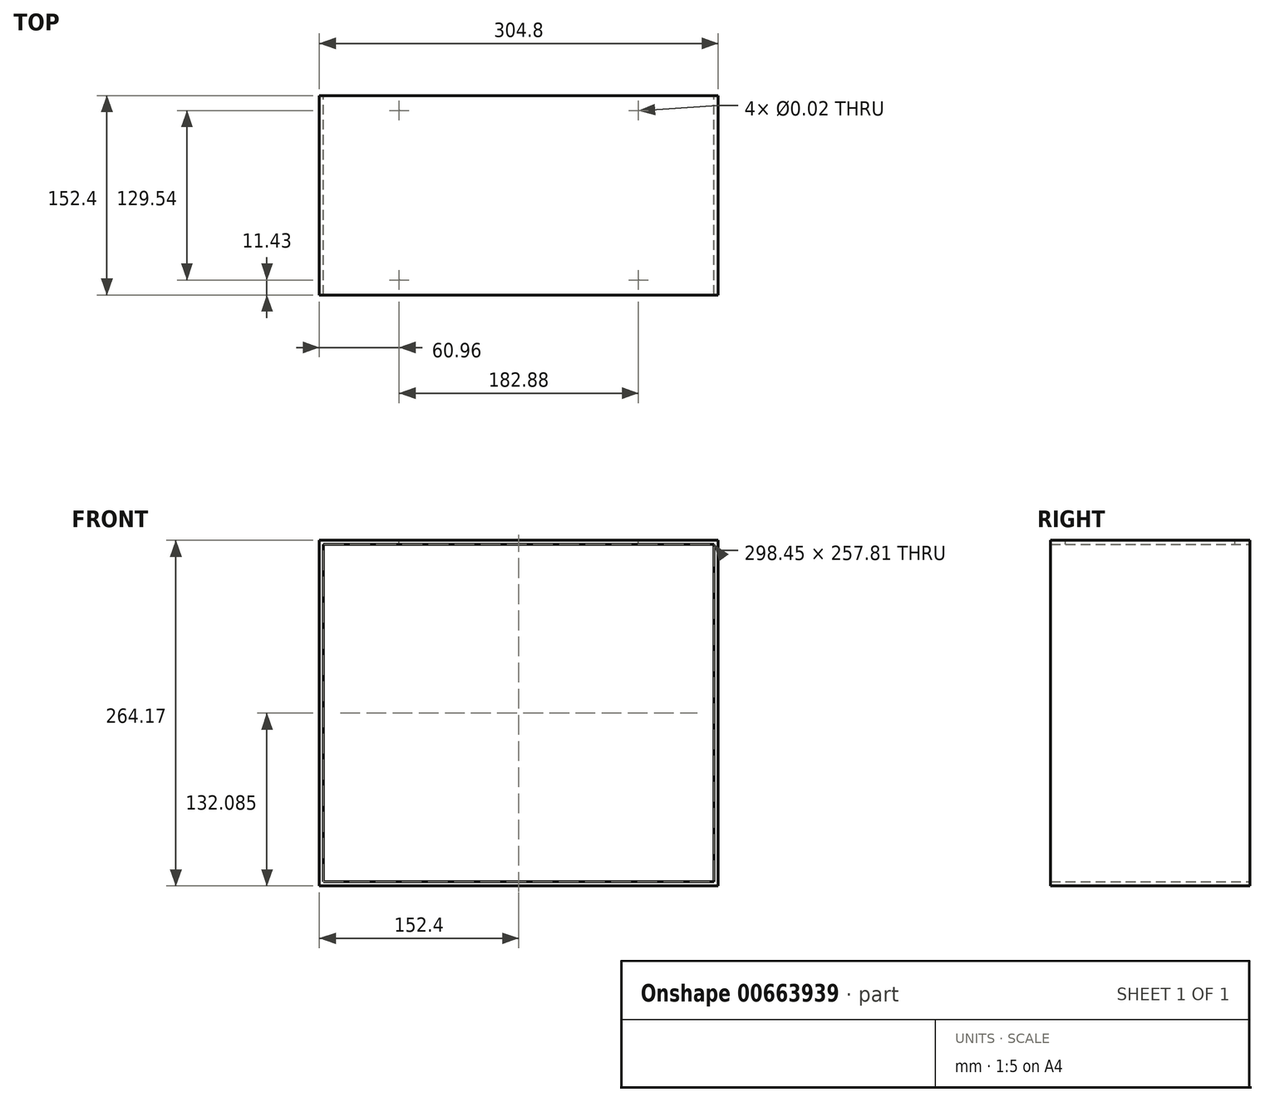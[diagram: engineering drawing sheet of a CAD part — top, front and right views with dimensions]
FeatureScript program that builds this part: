
annotation { "Feature Type Name" : "Feature", "Feature Type Description" : "" }
export const myFeature = defineFeature(function(context is Context, id is Id, definition is map)
    precondition{}
    {
        {
            var Q0;
            Q0=qCreatedBy(makeId("Top.planeOp"),FACE);
            var sketch = newSketch(context, id + "F0", { "sketchPlane" : qUnion([Q0])});
            skLineSegment(sketch, "E0.bottom", {"start": v(-152.4, 76.2) * mm, "end": v(152.4, 76.2) * mm});
            skLineSegment(sketch, "E0.top", {"start": v(-152.4, -76.2) * mm, "end": v(152.4, -76.2) * mm});
            skLineSegment(sketch, "E0.left", {"start": v(-152.4, 76.2) * mm, "end": v(-152.4, -76.2) * mm});
            skLineSegment(sketch, "E0.right", {"start": v(152.4, 76.2) * mm, "end": v(152.4, -76.2) * mm});
            skSolve(sketch);
        }
        {
            var Q0;
            Q0 = qSketchRegion(id + "F0", true);
            extrude(context, id + "F1", {"entities" : qUnion([Q0]), "depth" : 3.17 * mm, "offsetDistance" : 25.4 * mm});
        }
        {
            var Q0;
            Q0=makeQuery(id+"F1.opExtrude","CAP_FACE",FACE,{"disambiguationData":[OSD([sQuery(id+"F0.wireOp",EDGE,"E0.bottom"),sQuery(id+"F0.wireOp",EDGE,"E0.top"),sQuery(id+"F0.wireOp",EDGE,"E0.left"),sQuery(id+"F0.wireOp",EDGE,"E0.right")])],"isStart":false});
            var sketch = newSketch(context, id + "F2", { "sketchPlane" : qUnion([Q0])});
            skLineSegment(sketch, "E1.bottom", {"start": v(-107.95, 82.55) * mm, "end": v(107.95, 82.55) * mm});
            skLineSegment(sketch, "E1.top", {"start": v(-107.95, -82.55) * mm, "end": v(107.95, -82.55) * mm});
            skLineSegment(sketch, "E1.left", {"start": v(-107.95, 82.55) * mm, "end": v(-107.95, -82.55) * mm});
            skLineSegment(sketch, "E1.right", {"start": v(107.95, 82.55) * mm, "end": v(107.95, -82.55) * mm});
            skSolve(sketch);
        }
        {
            var Q0;
            {var subQ0=sQuery(id+"F2.wireOp",EDGE,"E1.left");var subQ1=makeQuery(id+"F1.opExtrude","CAP_EDGE",EDGE,{"disambiguationData":[OSD([sQuery(id+"F0.wireOp",EDGE,"E0.bottom")])],"isStart":false});var subQ2=makeQuery(id+"F2.imprint","INTERSECT",VERTEX,{"derivedFrom":[subQ1,subQ0]});Q0=makeQuery(id+"F2.imprint","IMPRINT",FACE,{"disambiguationData":[TD([[makeQuery(id+"F2.imprint","IMPRINT",EDGE,{"disambiguationData":[TD([[subQ2,-1.0]])],"derivedFrom":subQ0}),1.0]])]});}
            var sketch = newSketch(context, id + "F3", { "sketchPlane" : qUnion([Q0])});
            skPoint(sketch, "E2", {"position": v(-91.44, 64.77) * mm});
            skPoint(sketch, "E3", {"position": v(-91.44, -64.77) * mm});
            skPoint(sketch, "E4.MirrorP", {"position": v(91.44, -64.77) * mm});
            skPoint(sketch, "E5.MirrorP", {"position": v(91.44, 64.77) * mm});
            skSolve(sketch);
        }
        {
            var Q0;
            Q0=sQuery(id+"F3.wireOp",VERTEX,"E2");
            var Q1;
            Q1=sQuery(id+"F3.wireOp",VERTEX,"E3");
            var Q2;
            Q2=sQuery(id+"F3.wireOp",VERTEX,"E4.MirrorP");
            var Q3;
            Q3=sQuery(id+"F3.wireOp",VERTEX,"E5.MirrorP");
            var Q4;
            Q4=makeQuery(id+"F1.opExtrude","SWEPT_BODY",BODY,{"disambiguationData":[OSD([sQuery(id+"F0.wireOp",EDGE,"E0.bottom"),sQuery(id+"F0.wireOp",EDGE,"E0.top"),sQuery(id+"F0.wireOp",EDGE,"E0.left"),sQuery(id+"F0.wireOp",EDGE,"E0.right")])]});
            hole(context, id + "F4", {"style" : HoleStyle.SIMPLE, "endStyle" : HoleEndStyle.THROUGH, "standardTappedOrClearance" : lookupTablePath({ "standard" : "ANSI", "size" : "1/2 (0.5)", "type" : "Drilled" }), "standardBlindInLast" : lookupTablePath({ "standard" : "ANSI", "size" : "1/2", "type" : "Drilled" }), "holeDiameter" : 1 / 50.8 * mm, "majorDiameter" : 6.35 * mm, "isTappedThrough" : true, "tappedDepth" : 12.7 * mm, "tapClearance" : 3, "locations" : qUnion([Q0, Q1, Q2, Q3]), "scope" : qUnion([Q4])});
        }
        {
            var Q0;
            Q0=makeQuery(id+"F1.opExtrude","CAP_FACE",FACE,{"disambiguationData":[OSD([sQuery(id+"F0.wireOp",EDGE,"E0.bottom"),sQuery(id+"F0.wireOp",EDGE,"E0.top"),sQuery(id+"F0.wireOp",EDGE,"E0.left"),sQuery(id+"F0.wireOp",EDGE,"E0.right")])],"isStart":true});
            var sketch = newSketch(context, id + "F5", { "sketchPlane" : qUnion([Q0])});
            skLineSegment(sketch, "E6.bottom", {"start": v(-152.4, 76.2) * mm, "end": v(-149.22, 76.2) * mm});
            skLineSegment(sketch, "E6.top", {"start": v(-152.4, -76.2) * mm, "end": v(-149.22, -76.2) * mm});
            skLineSegment(sketch, "E6.left", {"start": v(-152.4, 76.2) * mm, "end": v(-152.4, -76.2) * mm});
            skLineSegment(sketch, "E6.right", {"start": v(-149.22, 76.2) * mm, "end": v(-149.22, -76.2) * mm});
            skLineSegment(sketch, "E7.MirrorCS", {"start": v(152.4, 76.2) * mm, "end": v(149.22, 76.2) * mm});
            skLineSegment(sketch, "E8.MirrorCS", {"start": v(152.4, -76.2) * mm, "end": v(149.22, -76.2) * mm});
            skLineSegment(sketch, "E9.MirrorCS", {"start": v(152.4, 76.2) * mm, "end": v(152.4, -76.2) * mm});
            skLineSegment(sketch, "E10.MirrorCS", {"start": v(149.22, 76.2) * mm, "end": v(149.22, -76.2) * mm});
            skSolve(sketch);
        }
        {
            var Q0;
            Q0 = qSketchRegion(id + "F5", true);
            extrude(context, id + "F6", {"entities" : qUnion([Q0]), "operationType" : NewBodyOperationType.ADD, "depth" : 257.8 * mm, "offsetDistance" : 25.4 * mm});
        }
        {
            var Q0;
            Q0=makeQuery(id+"F6.opExtrude","CAP_FACE",FACE,{"disambiguationData":[OSD([sQuery(id+"F5.wireOp",EDGE,"E6.bottom"),sQuery(id+"F5.wireOp",EDGE,"E6.top"),sQuery(id+"F5.wireOp",EDGE,"E6.left"),sQuery(id+"F5.wireOp",EDGE,"E6.right")])],"isStart":false});
            var sketch = newSketch(context, id + "F7", { "sketchPlane" : qUnion([Q0])});
            skPoint(sketch, "E11", {"position": v(-152.4, 76.2) * mm});
            skPoint(sketch, "E12", {"position": v(-152.4, -76.2) * mm});
            skPoint(sketch, "E13.MirrorP", {"position": v(152.4, 76.2) * mm});
            skPoint(sketch, "E14.MirrorP", {"position": v(152.4, -76.2) * mm});
            skLineSegment(sketch, "E15.bottom", {"start": v(-152.4, 76.2) * mm, "end": v(152.4, 76.2) * mm});
            skLineSegment(sketch, "E15.top", {"start": v(-152.4, -76.2) * mm, "end": v(152.4, -76.2) * mm});
            skLineSegment(sketch, "E15.left", {"start": v(-152.4, 76.2) * mm, "end": v(-152.4, -76.2) * mm});
            skLineSegment(sketch, "E15.right", {"start": v(152.4, 76.2) * mm, "end": v(152.4, -76.2) * mm});
            skSolve(sketch);
        }
        {
            var Q0;
            Q0 = qSketchRegion(id + "F7", true);
            extrude(context, id + "F8", {"entities" : qUnion([Q0]), "operationType" : NewBodyOperationType.ADD, "depth" : 3.17 * mm, "offsetDistance" : 25.4 * mm});
        }
    });
